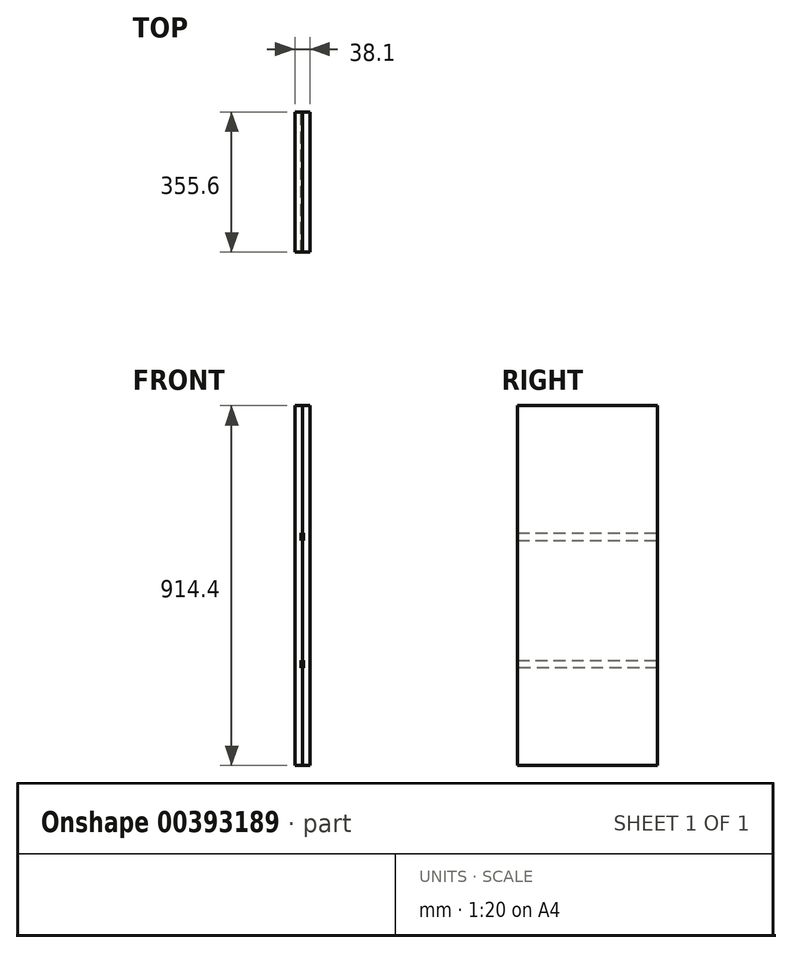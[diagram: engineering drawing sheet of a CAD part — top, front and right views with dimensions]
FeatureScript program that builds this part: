
annotation { "Feature Type Name" : "Feature", "Feature Type Description" : "" }
export const myFeature = defineFeature(function(context is Context, id is Id, definition is map)
    precondition{}
    {
        {
            var Q0;
            Q0=qCreatedBy(makeId("Right.planeOp"),FACE);
            var sketch = newSketch(context, id + "F0", { "sketchPlane" : qUnion([Q0])});
            skLineSegment(sketch, "E0.bottom", {"start": v(-3872.57, 3158.61) * mm, "end": v(-3516.97, 3158.61) * mm});
            skLineSegment(sketch, "E0.top", {"start": v(-3872.57, 2244.21) * mm, "end": v(-3516.97, 2244.21) * mm});
            skLineSegment(sketch, "E0.left", {"start": v(-3872.57, 3158.61) * mm, "end": v(-3872.57, 2244.21) * mm});
            skLineSegment(sketch, "E0.right", {"start": v(-3516.97, 3158.61) * mm, "end": v(-3516.97, 2244.21) * mm});
            skLineSegment(sketch, "E1.bottom", {"start": v(-3872.57, 2834.76) * mm, "end": v(-3516.97, 2834.76) * mm});
            skLineSegment(sketch, "E1.top", {"start": v(-3872.57, 2815.71) * mm, "end": v(-3516.97, 2815.71) * mm});
            skLineSegment(sketch, "E1.left", {"start": v(-3872.57, 2834.76) * mm, "end": v(-3872.57, 2815.71) * mm});
            skLineSegment(sketch, "E1.right", {"start": v(-3516.97, 2834.76) * mm, "end": v(-3516.97, 2815.71) * mm});
            skPoint(sketch, "E2.endSnap0", {"position": v(-3516.97, 2701.41) * mm});
            skLineSegment(sketch, "E3.MirrorCS", {"start": v(-3872.57, 2510.91) * mm, "end": v(-3516.97, 2510.91) * mm});
            skLineSegment(sketch, "E4", {"start": v(-3516.97, 2491.86) * mm, "end": v(-3872.57, 2491.86) * mm});
            skSolve(sketch);
        }
        {
            var Q0;
            {var subQ0=sQuery(id+"F0.wireOp",EDGE,"E0.bottom");Q0=makeQuery(id+"F0.imprint","IMPRINT",FACE,{"disambiguationData":[TD([[makeQuery(id+"F0.imprint","IMPRINT",EDGE,{"derivedFrom":subQ0}),-1.0]])]});}
            var Q1;
            {var subQ0=sQuery(id+"F0.wireOp",EDGE,"E0.top");Q1=makeQuery(id+"F0.imprint","IMPRINT",FACE,{"disambiguationData":[TD([[makeQuery(id+"F0.imprint","IMPRINT",EDGE,{"derivedFrom":subQ0}),1.0]])]});}
            var Q2;
            {var subQ0=sQuery(id+"F0.wireOp",EDGE,"E1.top");Q2=makeQuery(id+"F0.imprint","IMPRINT",FACE,{"disambiguationData":[TD([[makeQuery(id+"F0.imprint","IMPRINT",EDGE,{"derivedFrom":subQ0}),-1.0]])]});}
            var Q3;
            {var subQ0=sQuery(id+"F0.wireOp",EDGE,"E3.MirrorCS");Q3=makeQuery(id+"F0.imprint","IMPRINT",FACE,{"disambiguationData":[TD([[makeQuery(id+"F0.imprint","IMPRINT",EDGE,{"derivedFrom":subQ0}),-1.0]])]});}
            var Q4;
            Q4=makeQuery(id+"F0.imprint","IMPRINT",FACE,{"disambiguationData":[TD([[makeQuery(id+"F0.imprint","IMPRINT",EDGE,{"derivedFrom":sQuery(id+"F0.wireOp",EDGE,"E1.bottom")}),-1.0]])]});
            extrude(context, id + "F1", {"entities" : qUnion([Q0, Q1, Q2, Q3, Q4]), "depth" : 19.05 * mm});
        }
        {
            var Q0;
            Q0=makeQuery(id+"F0.imprint","IMPRINT",FACE,{"disambiguationData":[TD([[makeQuery(id+"F0.imprint","IMPRINT",EDGE,{"derivedFrom":sQuery(id+"F0.wireOp",EDGE,"E1.bottom")}),-1.0]])]});
            var Q1;
            {var subQ0=sQuery(id+"F0.wireOp",EDGE,"E3.MirrorCS");Q1=makeQuery(id+"F0.imprint","IMPRINT",FACE,{"disambiguationData":[TD([[makeQuery(id+"F0.imprint","IMPRINT",EDGE,{"derivedFrom":subQ0}),-1.0]])]});}
            extrude(context, id + "F2", {"entities" : qUnion([Q0, Q1]), "operationType" : NewBodyOperationType.REMOVE, "depth" : 3.17 * mm});
        }
        {
            var Q0;
            Q0=makeQuery(id+"F1.opExtrude","SWEPT_BODY",BODY,{"disambiguationData":[OSD([sQuery(id+"F0.wireOp",EDGE,"E0.bottom"),sQuery(id+"F0.wireOp",EDGE,"E0.top"),sQuery(id+"F0.wireOp",EDGE,"E0.left"),sQuery(id+"F0.wireOp",EDGE,"E0.right"),sQuery(id+"F0.wireOp",EDGE,"E1.left"),sQuery(id+"F0.wireOp",EDGE,"E1.right")])]});
            var Q1;
            Q1=qCreatedBy(makeId("Right.planeOp"),FACE);
            mirror(context, id + "F3", {"entities" : qUnion([Q0]), "mirrorPlane" : qUnion([Q1])});
        }
    });
